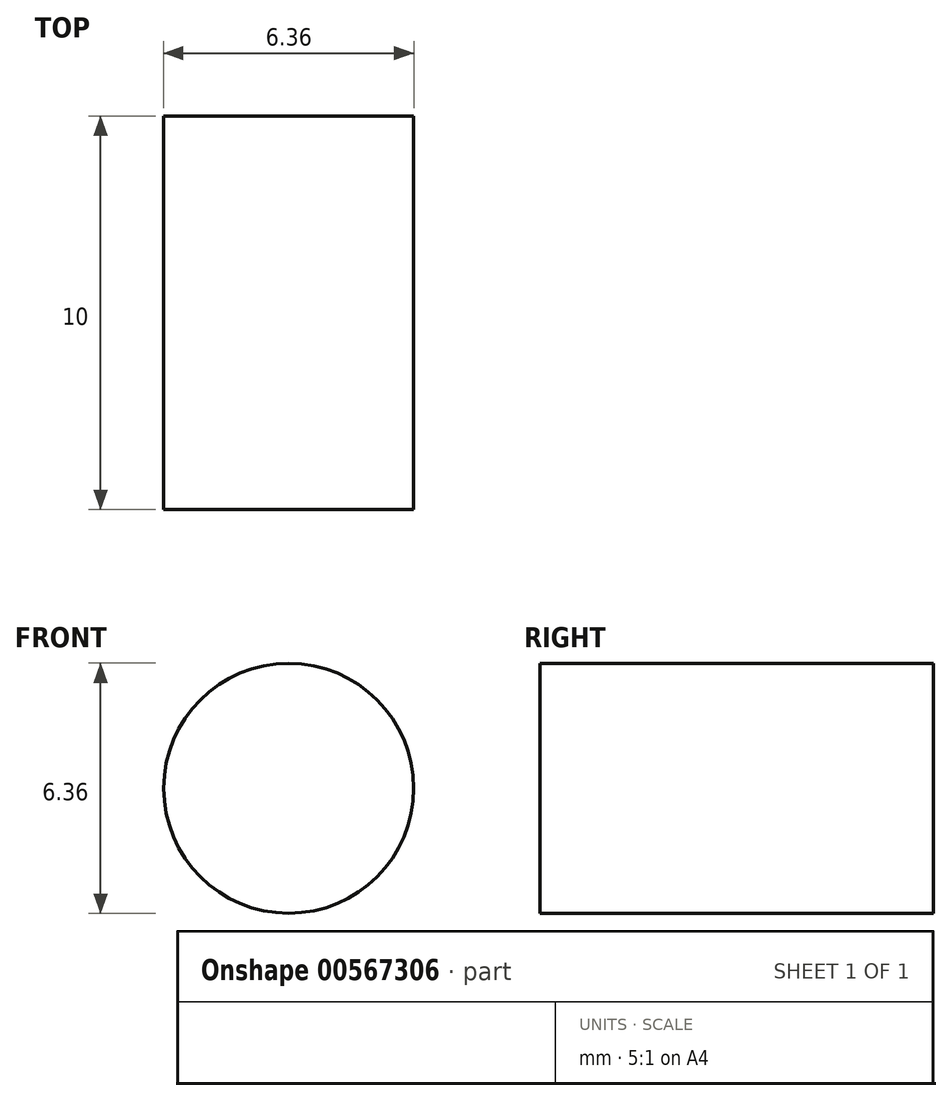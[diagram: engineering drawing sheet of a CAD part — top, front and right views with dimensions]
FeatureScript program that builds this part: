
annotation { "Feature Type Name" : "Feature", "Feature Type Description" : "" }
export const myFeature = defineFeature(function(context is Context, id is Id, definition is map)
    precondition{}
    {
        {
            var Q0;
            Q0=qCreatedBy(makeId("Front.planeOp"),FACE);
            var sketch = newSketch(context, id + "F0", { "sketchPlane" : qUnion([Q0])});
            skCircle(sketch, "E0", {"center": v(0, 0) * mm, "radius": 3.18 * mm});
            skSolve(sketch);
        }
        {
            var Q0;
            Q0=makeQuery(id+"F0.imprint","IMPRINT",FACE,{"disambiguationData":[TD([[makeQuery(id+"F0.imprint","IMPRINT",EDGE,{"derivedFrom":sQuery(id+"F0.wireOp",EDGE,"E0")}),1.0]])]});
            extrude(context, id + "F1", {"entities" : qUnion([Q0]), "depth" : 10 * mm, "offsetDistance" : 25.4 * mm});
        }
    });
